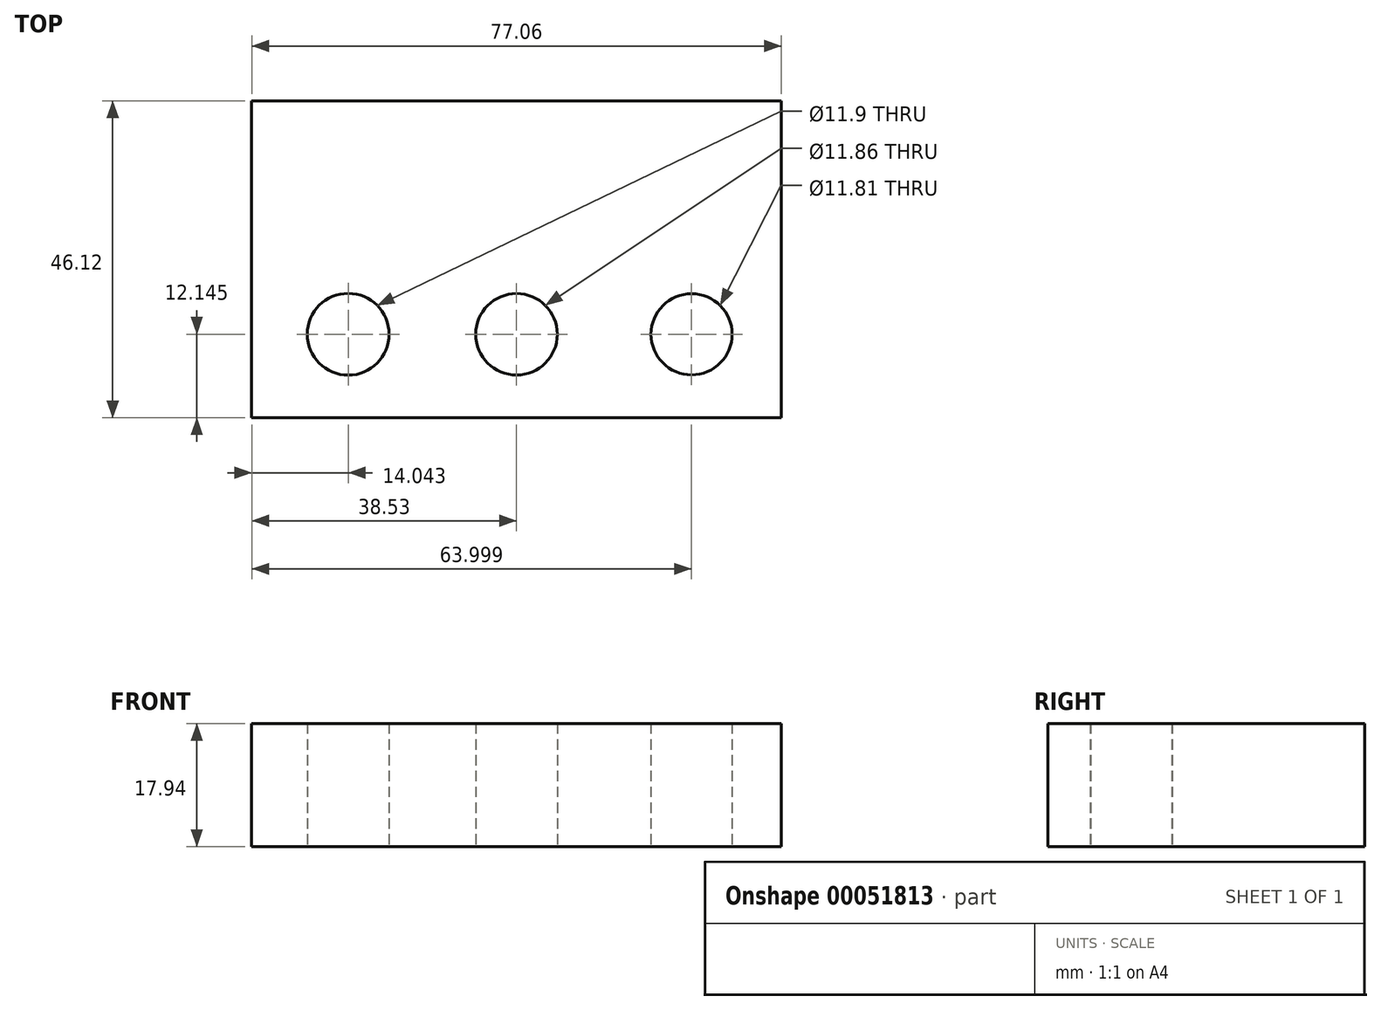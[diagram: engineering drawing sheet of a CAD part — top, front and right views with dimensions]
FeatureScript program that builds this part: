
annotation { "Feature Type Name" : "Feature", "Feature Type Description" : "" }
export const myFeature = defineFeature(function(context is Context, id is Id, definition is map)
    precondition{}
    {
        {
            var Q0;
            Q0=qCreatedBy(makeId("Top.planeOp"),FACE);
            var sketch = newSketch(context, id + "F0", { "sketchPlane" : qUnion([Q0])});
            skLineSegment(sketch, "E0.rect.bottom", {"start": v(38.53, -23.06) * mm, "end": v(-38.53, -23.06) * mm});
            skLineSegment(sketch, "E0.rect.top", {"start": v(38.53, 23.06) * mm, "end": v(-38.53, 23.06) * mm});
            skLineSegment(sketch, "E0.rect.left", {"start": v(38.53, -23.06) * mm, "end": v(38.53, 23.06) * mm});
            skLineSegment(sketch, "E0.rect.right", {"start": v(-38.53, -23.06) * mm, "end": v(-38.53, 23.06) * mm});
            skPoint(sketch, "E0.rect.middle", {"position": v(0, 0) * mm});
            skCircle(sketch, "E1", {"center": v(-24.49, 10.91) * mm, "radius": 5.95 * mm});
            skCircle(sketch, "E2", {"center": v(0, 10.91) * mm, "radius": 5.93 * mm});
            skCircle(sketch, "E3", {"center": v(25.47, 10.91) * mm, "radius": 5.9 * mm});
            skCircle(sketch, "E4.MirrorC", {"center": v(-24.49, -10.91) * mm, "radius": 5.95 * mm});
            skCircle(sketch, "E5.MirrorC", {"center": v(0, -10.91) * mm, "radius": 5.93 * mm});
            skCircle(sketch, "E6.MirrorC", {"center": v(25.47, -10.91) * mm, "radius": 5.9 * mm});
            skSolve(sketch);
        }
        {
            var Q0;
            Q0 = qSketchRegion(id + "F0", true);
            extrude(context, id + "F1", {"entities" : qUnion([Q0]), "depth" : 22.86 * mm});
        }
        {
            var Q0;
            Q0=makeQuery(id+"F0.imprint","IMPRINT",FACE,{"disambiguationData":[TD([[makeQuery(id+"F0.imprint","IMPRINT",EDGE,{"derivedFrom":sQuery(id+"F0.wireOp",EDGE,"E1")}),1.0]])]});
            var Q1;
            Q1=makeQuery(id+"F0.imprint","IMPRINT",FACE,{"disambiguationData":[TD([[makeQuery(id+"F0.imprint","IMPRINT",EDGE,{"derivedFrom":sQuery(id+"F0.wireOp",EDGE,"E2")}),1.0]])]});
            var Q2;
            Q2=makeQuery(id+"F0.imprint","IMPRINT",FACE,{"disambiguationData":[TD([[makeQuery(id+"F0.imprint","IMPRINT",EDGE,{"derivedFrom":sQuery(id+"F0.wireOp",EDGE,"E3")}),1.0]])]});
            var Q3;
            Q3=makeQuery(id+"F0.imprint","IMPRINT",FACE,{"disambiguationData":[TD([[makeQuery(id+"F0.imprint","IMPRINT",EDGE,{"derivedFrom":sQuery(id+"F0.wireOp",EDGE,"E6.MirrorC")}),-1.0]])]});
            var Q4;
            Q4=makeQuery(id+"F0.imprint","IMPRINT",FACE,{"disambiguationData":[TD([[makeQuery(id+"F0.imprint","IMPRINT",EDGE,{"derivedFrom":sQuery(id+"F0.wireOp",EDGE,"E5.MirrorC")}),-1.0]])]});
            var Q5;
            Q5=makeQuery(id+"F0.imprint","IMPRINT",FACE,{"disambiguationData":[TD([[makeQuery(id+"F0.imprint","IMPRINT",EDGE,{"derivedFrom":sQuery(id+"F0.wireOp",EDGE,"E4.MirrorC")}),-1.0]])]});
            extrude(context, id + "F2", {"entities" : qUnion([Q0, Q1, Q2, Q3, Q4, Q5]), "operationType" : NewBodyOperationType.ADD, "depth" : 27.94 * mm});
        }
        {
            var Q0;
            Q0=makeQuery(id+"F0.imprint","IMPRINT",FACE,{"disambiguationData":[TD([[makeQuery(id+"F0.imprint","IMPRINT",EDGE,{"derivedFrom":sQuery(id+"F0.wireOp",EDGE,"E1")}),1.0]])]});
            var Q1;
            Q1=makeQuery(id+"F0.imprint","IMPRINT",FACE,{"disambiguationData":[TD([[makeQuery(id+"F0.imprint","IMPRINT",EDGE,{"derivedFrom":sQuery(id+"F0.wireOp",EDGE,"E4.MirrorC")}),-1.0]])]});
            var Q2;
            Q2=makeQuery(id+"F0.imprint","IMPRINT",FACE,{"disambiguationData":[TD([[makeQuery(id+"F0.imprint","IMPRINT",EDGE,{"derivedFrom":sQuery(id+"F0.wireOp",EDGE,"E5.MirrorC")}),-1.0]])]});
            var Q3;
            Q3=makeQuery(id+"F0.imprint","IMPRINT",FACE,{"disambiguationData":[TD([[makeQuery(id+"F0.imprint","IMPRINT",EDGE,{"derivedFrom":sQuery(id+"F0.wireOp",EDGE,"E2")}),1.0]])]});
            var Q4;
            Q4=makeQuery(id+"F0.imprint","IMPRINT",FACE,{"disambiguationData":[TD([[makeQuery(id+"F0.imprint","IMPRINT",EDGE,{"derivedFrom":sQuery(id+"F0.wireOp",EDGE,"E3")}),1.0]])]});
            var Q5;
            Q5=makeQuery(id+"F0.imprint","IMPRINT",FACE,{"disambiguationData":[TD([[makeQuery(id+"F0.imprint","IMPRINT",EDGE,{"derivedFrom":sQuery(id+"F0.wireOp",EDGE,"E6.MirrorC")}),-1.0]])]});
            extrude(context, id + "F3", {"entities" : qUnion([Q0, Q1, Q2, Q3, Q4, Q5]), "operationType" : NewBodyOperationType.ADD, "endBound" : BoundingType.UP_TO_NEXT, "depth" : 25 * mm});
        }
        {
            var Q0;
            Q0=makeQuery(id+"F0.imprint","IMPRINT",FACE,{"disambiguationData":[TD([[makeQuery(id+"F0.imprint","IMPRINT",EDGE,{"derivedFrom":sQuery(id+"F0.wireOp",EDGE,"E4.MirrorC")}),-1.0]])]});
            var Q1;
            Q1=makeQuery(id+"F0.imprint","IMPRINT",FACE,{"disambiguationData":[TD([[makeQuery(id+"F0.imprint","IMPRINT",EDGE,{"derivedFrom":sQuery(id+"F0.wireOp",EDGE,"E5.MirrorC")}),-1.0]])]});
            var Q2;
            Q2=makeQuery(id+"F0.imprint","IMPRINT",FACE,{"disambiguationData":[TD([[makeQuery(id+"F0.imprint","IMPRINT",EDGE,{"derivedFrom":sQuery(id+"F0.wireOp",EDGE,"E6.MirrorC")}),-1.0]])]});
            var Q3;
            Q3=makeQuery(id+"F0.imprint","IMPRINT",FACE,{"disambiguationData":[TD([[makeQuery(id+"F0.imprint","IMPRINT",EDGE,{"derivedFrom":sQuery(id+"F0.wireOp",EDGE,"E3")}),1.0]])]});
            var Q4;
            Q4=makeQuery(id+"F0.imprint","IMPRINT",FACE,{"disambiguationData":[TD([[makeQuery(id+"F0.imprint","IMPRINT",EDGE,{"derivedFrom":sQuery(id+"F0.wireOp",EDGE,"E2")}),1.0]])]});
            var Q5;
            Q5=makeQuery(id+"F0.imprint","IMPRINT",FACE,{"disambiguationData":[TD([[makeQuery(id+"F0.imprint","IMPRINT",EDGE,{"derivedFrom":sQuery(id+"F0.wireOp",EDGE,"E1")}),1.0]])]});
            extrude(context, id + "F4", {"entities" : qUnion([Q0, Q1, Q2, Q3, Q4, Q5]), "operationType" : NewBodyOperationType.REMOVE, "depth" : 10 * mm});
        }
    });
